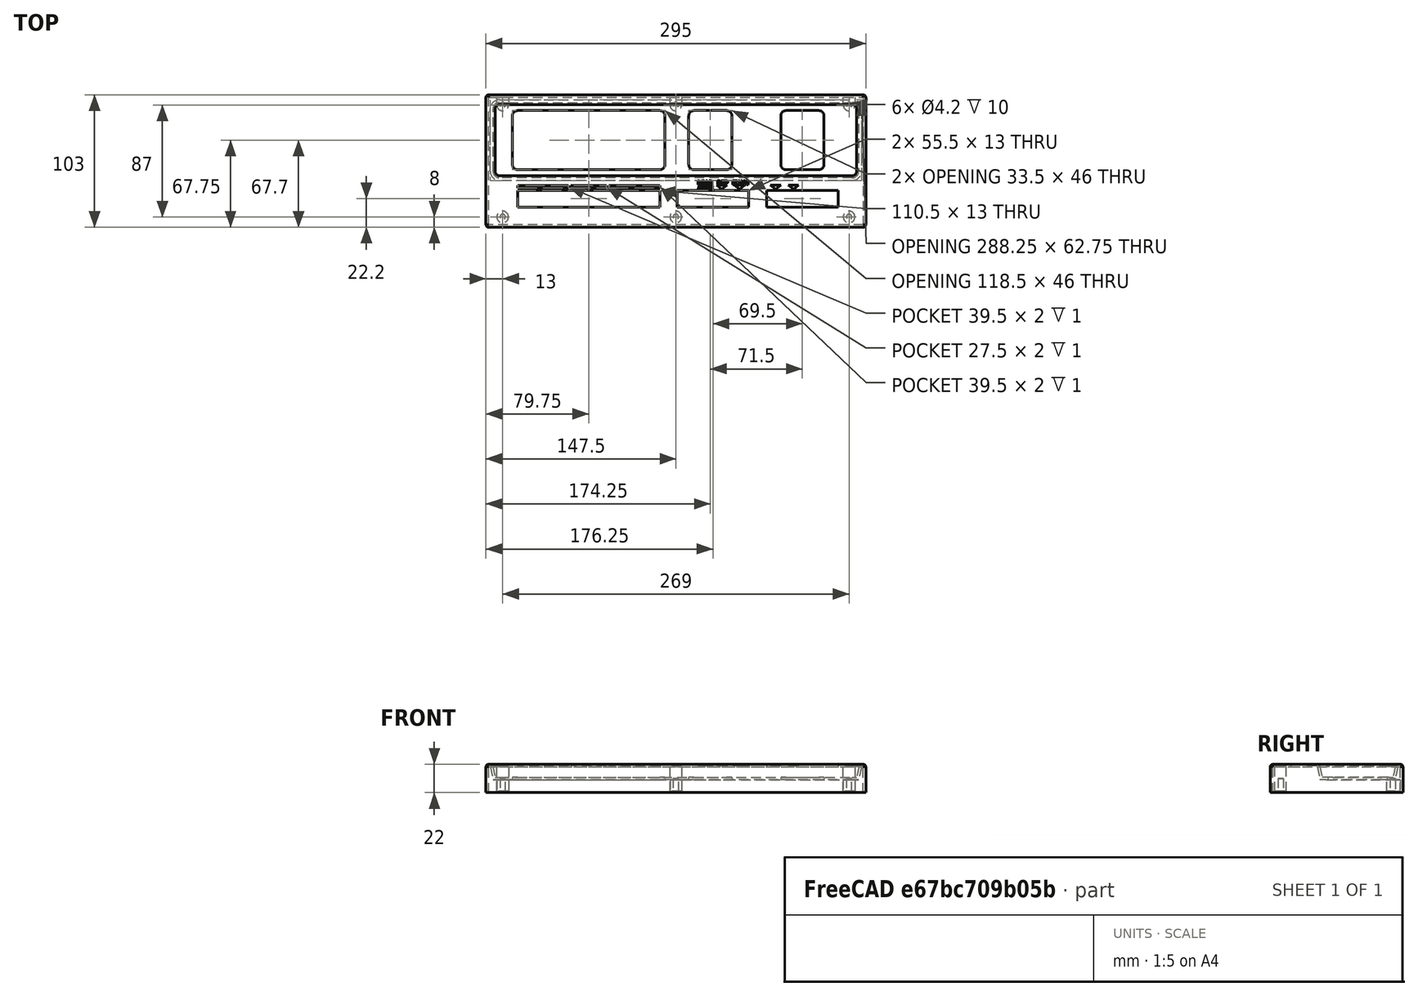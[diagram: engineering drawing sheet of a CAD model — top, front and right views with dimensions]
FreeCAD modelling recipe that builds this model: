
FCSTD DOCUMENT  (FreeCAD 0.21R33771 (Git))
Label: front panel
License: All rights reserved
LicenseURL: http://en.wikipedia.org/wiki/All_rights_reserved
objects: PartDesign::Pocket×8, Sketcher::SketchObject×7, PartDesign::LinearPattern×4, Part::Part2DObjectPython×4, PartDesign::Pad×3, TechDraw::DrawViewDimension×3, PartDesign::Draft×1, PartDesign::Thickness×1, PartDesign::MultiTransform×1, TechDraw::DrawSVGTemplate×1, PartDesign::Body×1, TechDraw::DrawProjGroupItem×1, TechDraw::DrawProjGroup×1, TechDraw::DrawPage×1
note: 48 computed .brp shape members not serialized (recipe doc carries the construction recipe); baked Part::Feature solids carry a one-line shape summary decoded from their .brp

FEATURE [Sketcher::SketchObject] Sketch
  FullyConstrained = true
  MapMode = 5
  Support = -> [XY_Plane]
  sketch-geometry (4):
    g0: LineSegment StartX=-145.5 StartY=49.5 StartZ=0 EndX=145.5 EndY=49.5 EndZ=0
    g1: LineSegment StartX=145.5 StartY=49.5 StartZ=0 EndX=145.5 EndY=-49.5 EndZ=0
    g2: LineSegment StartX=145.5 StartY=-49.5 StartZ=0 EndX=-145.5 EndY=-49.5 EndZ=0
    g3: LineSegment StartX=-145.5 StartY=-49.5 StartZ=0 EndX=-145.5 EndY=49.5 EndZ=0
  constraints (11):
    c: Coincident(g0,g1)
    c: Coincident(g1,g2)
    c: Coincident(g2,g3)
    c: Coincident(g3,g0)
    c: Horizontal(g0)
    c: Horizontal(g2)
    c: Vertical(g1)
    c: Vertical(g3)
    c: Symmetric(g1,g0,g-1)
    c: DistanceY(g3,g3) = 99
    c: DistanceX(g0,g0) = 291
FEATURE [PartDesign::Pad] Pad
  Direction = (0,0,1)
  Length = 20
  Length2 = 10
  Profile = -> Sketch
  ReferenceAxis = -> Sketch [N_Axis]
  Type = 0
FEATURE [Sketcher::SketchObject] Sketch001
  FullyConstrained = true
  MapMode = 5
  Placement = pos=(0,0,20) rot=(0,0,1;0rad)
  Support = -> [Pad]
  sketch-geometry (10):
    g0: ArcOfCircle CenterX=-137 CenterY=40.5 CenterZ=0 NormalX=0 NormalY=0 NormalZ=1 AngleXU=0 Radius=5 StartAngle=1.5708 EndAngle=3.14159
    g1: LineSegment StartX=-137 StartY=45.5 StartZ=0 EndX=137 EndY=45.5 EndZ=0
    g2: ArcOfCircle CenterX=137 CenterY=40.5 CenterZ=0 NormalX=0 NormalY=0 NormalZ=1 AngleXU=0 Radius=5 StartAngle=5e-16 EndAngle=1.5708
    g3: LineSegment StartX=142 StartY=40.5 StartZ=0 EndX=142 EndY=-8 EndZ=0
    g4: ArcOfCircle CenterX=137 CenterY=-8 CenterZ=0 NormalX=0 NormalY=0 NormalZ=1 AngleXU=0 Radius=5 StartAngle=4.71239 EndAngle=6.28319
    g5: LineSegment StartX=137 StartY=-13 StartZ=0 EndX=-137 EndY=-13 EndZ=0
    g6: ArcOfCircle CenterX=-137 CenterY=-8 CenterZ=0 NormalX=0 NormalY=0 NormalZ=1 AngleXU=0 Radius=5 StartAngle=3.14159 EndAngle=4.71239
    g7: LineSegment StartX=-142 StartY=-8 StartZ=0 EndX=-142 EndY=40.5 EndZ=0
    g8: GeomPoint X=-142 Y=45.5 Z=0
    g9: GeomPoint X=142 Y=-13 Z=0
  constraints (23):
    c: Tangent(g0,g1) = 1.5708
    c: Tangent(g1,g2) = 1.5708
    c: Tangent(g2,g3) = 1.5708
    c: Tangent(g3,g4) = 1.5708
    c: Tangent(g4,g5) = 1.5708
    c: Tangent(g5,g6) = 1.5708
    c: Tangent(g6,g7) = 1.5708
    c: Tangent(g7,g0) = 1.5708
    c: Horizontal(g1)
    c: Horizontal(g5)
    c: Vertical(g3)
    c: Vertical(g7)
    c: Equal(g2,g4)
    c: Equal(g4,g6)
    c: PointOnObject(g8,g1)
    c: PointOnObject(g8,g7)
    c: PointOnObject(g9,g3)
    c: PointOnObject(g9,g5)
    c: Diameter(g2) = 10
    c: DistanceX(g0,g2) = 284
    c: Symmetric(g0,g2,g-2)
    c: DistanceY(g-1,g0) = 45.5
    c: DistanceY(g5,g-1) = 13
FEATURE [PartDesign::Pocket] Pocket
  BaseFeature = -> Pad
  Direction = (0,0,-1)
  Length = 10
  Length2 = 5
  Profile = -> Sketch001
  ReferenceAxis = -> Sketch001 [N_Axis]
  Type = 0
FEATURE [PartDesign::Draft] Draft
  Angle = 12
  Base = -> Pocket [Face10]
  BaseFeature = -> Pocket
  NeutralPlane = -> Pocket [Face15]
  SupportTransform = false
FEATURE [PartDesign::Thickness] Thickness
  Base = -> Draft [Face4]
  BaseFeature = -> Draft
  Intersection = false
  Join = 0
  Mode = 0
  SupportTransform = false
  Value = 2
FEATURE [Sketcher::SketchObject] Sketch002
  FullyConstrained = true
  MapMode = 5
  Placement = pos=(0,0,22) rot=(0,0,1;0rad)
  Support = -> [Thickness]
  sketch-geometry (42):
    g0: LineSegment StartX=-123 StartY=-22.8 StartZ=0 EndX=-12.5 EndY=-22.8 EndZ=0
    g1: LineSegment StartX=-12.5 StartY=-22.8 StartZ=0 EndX=-12.5 EndY=-35.8 EndZ=0
    g2: LineSegment StartX=-12.5 StartY=-35.8 StartZ=0 EndX=-123 EndY=-35.8 EndZ=0
    g3: LineSegment StartX=-123 StartY=-35.8 StartZ=0 EndX=-123 EndY=-22.8 EndZ=0
    g4: LineSegment StartX=1 StartY=-22.8 StartZ=0 EndX=56.5 EndY=-22.8 EndZ=0
    g5: LineSegment StartX=56.5 StartY=-22.8 StartZ=0 EndX=56.5 EndY=-35.8 EndZ=0
    g6: LineSegment StartX=56.5 StartY=-35.8 StartZ=0 EndX=1 EndY=-35.8 EndZ=0
    g7: LineSegment StartX=1 StartY=-35.8 StartZ=0 EndX=1 EndY=-22.8 EndZ=0
    g8: LineSegment StartX=70.5 StartY=-22.8 StartZ=0 EndX=126 EndY=-22.8 EndZ=0
    g9: LineSegment StartX=126 StartY=-22.8 StartZ=0 EndX=126 EndY=-35.8 EndZ=0
    g10: LineSegment StartX=126 StartY=-35.8 StartZ=0 EndX=70.5 EndY=-35.8 EndZ=0
    g11: LineSegment StartX=70.5 StartY=-35.8 StartZ=0 EndX=70.5 EndY=-22.8 EndZ=0
    g12: ArcOfCircle CenterX=-123 CenterY=35.2 CenterZ=0 NormalX=0 NormalY=0 NormalZ=1 AngleXU=0 Radius=4 StartAngle=1.5708 EndAngle=3.14159
    g13: LineSegment StartX=-123 StartY=39.2 StartZ=0 EndX=-12.5 EndY=39.2 EndZ=0
    g14: ArcOfCircle CenterX=-12.5 CenterY=35.2 CenterZ=0 NormalX=0 NormalY=0 NormalZ=1 AngleXU=0 Radius=4 StartAngle=1e-15 EndAngle=1.5708
    g15: LineSegment StartX=-8.5 StartY=35.2 StartZ=0 EndX=-8.5 EndY=-2.8 EndZ=0
    g16: ArcOfCircle CenterX=-12.5 CenterY=-2.8 CenterZ=0 NormalX=0 NormalY=0 NormalZ=1 AngleXU=0 Radius=4 StartAngle=4.71239 EndAngle=6.28319
    g17: LineSegment StartX=-12.5 StartY=-6.8 StartZ=0 EndX=-123 EndY=-6.8 EndZ=0
    g18: ArcOfCircle CenterX=-123 CenterY=-2.8 CenterZ=0 NormalX=0 NormalY=0 NormalZ=1 AngleXU=0 Radius=4 StartAngle=3.14159 EndAngle=4.71239
    g19: LineSegment StartX=-127 StartY=-2.8 StartZ=0 EndX=-127 EndY=35.2 EndZ=0
    g20: GeomPoint X=-127 Y=39.2 Z=0
    g21: GeomPoint X=-8.5 Y=-6.8 Z=0
    g22: ArcOfCircle CenterX=14 CenterY=35.2 CenterZ=0 NormalX=0 NormalY=0 NormalZ=1 AngleXU=0 Radius=4 StartAngle=1.5708 EndAngle=3.14159
    g23: LineSegment StartX=14 StartY=39.2 StartZ=0 EndX=39.5 EndY=39.2 EndZ=0
    g24: ArcOfCircle CenterX=39.5 CenterY=35.2 CenterZ=0 NormalX=0 NormalY=0 NormalZ=1 AngleXU=0 Radius=4 StartAngle=1e-15 EndAngle=1.5708
    g25: LineSegment StartX=43.5 StartY=35.2 StartZ=0 EndX=43.5 EndY=-2.8 EndZ=0
    g26: ArcOfCircle CenterX=39.5 CenterY=-2.8 CenterZ=0 NormalX=0 NormalY=0 NormalZ=1 AngleXU=0 Radius=4 StartAngle=4.71239 EndAngle=6.28319
    g27: LineSegment StartX=39.5 StartY=-6.8 StartZ=0 EndX=14 EndY=-6.8 EndZ=0
    g28: ArcOfCircle CenterX=14 CenterY=-2.8 CenterZ=0 NormalX=0 NormalY=0 NormalZ=1 AngleXU=0 Radius=4 StartAngle=3.14159 EndAngle=4.71239
    g29: LineSegment StartX=10 StartY=-2.8 StartZ=0 EndX=10 EndY=35.2 EndZ=0
    g30: GeomPoint X=10 Y=39.2 Z=0
    g31: GeomPoint X=43.5 Y=-6.8 Z=0
    g32: ArcOfCircle CenterX=85.5 CenterY=35.2 CenterZ=0 NormalX=0 NormalY=0 NormalZ=1 AngleXU=0 Radius=4 StartAngle=1.5708 EndAngle=3.14159
    g33: LineSegment StartX=85.5 StartY=39.2 StartZ=0 EndX=111 EndY=39.2 EndZ=0
    g34: ArcOfCircle CenterX=111 CenterY=35.2 CenterZ=0 NormalX=0 NormalY=0 NormalZ=1 AngleXU=0 Radius=4 StartAngle=1e-15 EndAngle=1.5708
    g35: LineSegment StartX=115 StartY=35.2 StartZ=0 EndX=115 EndY=-2.8 EndZ=0
    g36: ArcOfCircle CenterX=111 CenterY=-2.8 CenterZ=0 NormalX=0 NormalY=0 NormalZ=1 AngleXU=0 Radius=4 StartAngle=4.71239 EndAngle=6.28319
    g37: LineSegment StartX=111 StartY=-6.8 StartZ=0 EndX=85.5 EndY=-6.8 EndZ=0
    g38: ArcOfCircle CenterX=85.5 CenterY=-2.8 CenterZ=0 NormalX=0 NormalY=0 NormalZ=1 AngleXU=0 Radius=4 StartAngle=3.14159 EndAngle=4.71239
    g39: LineSegment StartX=81.5 StartY=-2.8 StartZ=0 EndX=81.5 EndY=35.2 EndZ=0
    g40: GeomPoint X=81.5 Y=39.2 Z=0
    g41: GeomPoint X=115 Y=-6.8 Z=0
  constraints (108):
    c: Coincident(g0,g1)
    c: Coincident(g1,g2)
    c: Coincident(g2,g3)
    c: Coincident(g3,g0)
    c: Horizontal(g0)
    c: Horizontal(g2)
    c: Vertical(g1)
    c: Vertical(g3)
    c: Coincident(g4,g5)
    c: Coincident(g5,g6)
    c: Coincident(g6,g7)
    c: Coincident(g7,g4)
    c: Horizontal(g4)
    c: Horizontal(g6)
    c: Vertical(g5)
    c: Vertical(g7)
    c: Coincident(g8,g9)
    c: Coincident(g9,g10)
    c: Coincident(g10,g11)
    c: Coincident(g11,g8)
    c: Horizontal(g8)
    c: Horizontal(g10)
    c: Vertical(g9)
    c: Vertical(g11)
    c: Horizontal(g10,g5)
    c: Horizontal(g5,g1)
    c: Horizontal(g4,g0)
    c: Horizontal(g0,g8)
    c: DistanceY(g3,g3) = 13
    c: DistanceX(g2,g-1) = 123
    c: DistanceX(g0,g0) = 110.5
    c: DistanceY(g1,g-1) = 35.8
    c: DistanceX(g0,g4) = 13.5
    c: DistanceX(g4,g4) = 55.5
    c: DistanceX(g4,g8) = 14
    c: Equal(g8,g4)
    c: Tangent(g12,g13) = 1.5708
    c: Tangent(g13,g14) = 1.5708
    c: Tangent(g14,g15) = 1.5708
    c: Tangent(g15,g16) = 1.5708
    c: Tangent(g16,g17) = 1.5708
    c: Tangent(g17,g18) = 1.5708
    c: Tangent(g18,g19) = 1.5708
    c: Tangent(g19,g12) = 1.5708
    c: Horizontal(g13)
    c: Horizontal(g17)
    c: Vertical(g15)
    c: Vertical(g19)
    c: Equal(g12,g14)
    c: Equal(g14,g16)
    c: Equal(g16,g18)
    c: PointOnObject(g20,g13)
    c: PointOnObject(g20,g19)
    c: PointOnObject(g21,g15)
    c: PointOnObject(g21,g17)
    c: Radius(g12) = 4
    c: Vertical(g17,g0)
    c: Vertical(g16,g0)
    c: Tangent(g22,g23) = 1.5708
    c: Tangent(g23,g24) = 1.5708
    c: Tangent(g24,g25) = 1.5708
    c: Tangent(g25,g26) = 1.5708
    c: Tangent(g26,g27) = 1.5708
    c: Tangent(g27,g28) = 1.5708
    c: Tangent(g28,g29) = 1.5708
    c: Tangent(g29,g22) = 1.5708
    c: Horizontal(g23)
    c: Horizontal(g27)
    c: Vertical(g25)
    c: Vertical(g29)
    c: Equal(g22,g24)
    c: Equal(g24,g26)
    c: Equal(g26,g28)
    c: PointOnObject(g30,g23)
    c: PointOnObject(g30,g29)
    c: PointOnObject(g31,g25)
    c: PointOnObject(g31,g27)
    c: Equal(g26,g14)
    c: Horizontal(g22,g13)
    c: Horizontal(g27,g16)
    c: DistanceX(g26,g4) = 17
    c: DistanceX(g4,g27) = 13
    c: Tangent(g32,g33) = 1.5708
    c: Tangent(g33,g34) = 1.5708
    c: Tangent(g34,g35) = 1.5708
    c: Tangent(g35,g36) = 1.5708
    c: Tangent(g36,g37) = 1.5708
    c: Tangent(g37,g38) = 1.5708
    c: Tangent(g38,g39) = 1.5708
    c: Tangent(g39,g32) = 1.5708
    c: Horizontal(g33)
    c: Horizontal(g37)
    c: Vertical(g35)
    c: Vertical(g39)
    c: Equal(g32,g34)
    c: Equal(g34,g36)
    c: Equal(g36,g38)
    c: PointOnObject(g40,g33)
    c: PointOnObject(g40,g39)
    c: PointOnObject(g41,g35)
    c: PointOnObject(g41,g37)
    c: Horizontal(g23,g32)
    c: Equal(g32,g24)
    c: DistanceX(g36,g8) = 15
    c: Equal(g27,g37)
    c: DistanceY(g8,g35) = 20
    c: DistanceY(g8,g33) = 62
    c: Horizontal(g37,g16)
FEATURE [PartDesign::Pocket] Pocket001  label="Switch cut out"
  BaseFeature = -> Thickness
  Direction = (0,0,-1)
  Length = 5
  Length2 = 5
  Profile = -> Sketch002
  ReferenceAxis = -> Sketch002 [N_Axis]
  Type = 1
FEATURE [Sketcher::SketchObject] Sketch003
  FullyConstrained = true
  MapMode = 5
  Placement = pos=(0,0,20) rot=(1,0,0;3.14159rad)
  Support = -> [Pocket001]
  sketch-geometry (1):
    g0: Circle CenterX=-134.5 CenterY=43.5 CenterZ=0 NormalX=0 NormalY=0 NormalZ=1 AngleXU=0 Radius=4.5
  constraints (3):
    c: DistanceY(g-1,g0) = 43.5
    c: DistanceX(g0,g-1) = 134.5
    c: Diameter(g0) = 9
FEATURE [PartDesign::Pad] Pad001
  BaseFeature = -> Pocket001
  Direction = (0,0,-1)
  Length = 19
  Length2 = 10
  Profile = -> Sketch003
  ReferenceAxis = -> Sketch003 [N_Axis]
  Type = 0
FEATURE [PartDesign::LinearPattern] LinearPattern
  BaseFeature = -> Pad001
  Direction = -> Sketch003 [H_Axis]
  Length = 269
  Occurrences = 3
  Originals = -> [Pad001]
FEATURE [Sketcher::SketchObject] Sketch004
  ExternalGeometry = -> [LinearPattern]
  FullyConstrained = true
  MapMode = 5
  Placement = pos=(0,0,10) rot=(1,0,0;3.14159rad)
  Support = -> [LinearPattern]
  sketch-geometry (4):
    g0: ArcOfCircle CenterX=-134.5 CenterY=-43.5 CenterZ=0 NormalX=0 NormalY=0 NormalZ=1 AngleXU=0 Radius=4.5 StartAngle=-9e-16 EndAngle=3.14159
    g1: LineSegment StartX=-139 StartY=-43.5 StartZ=0 EndX=-139 EndY=-49.5 EndZ=0
    g2: LineSegment StartX=-139 StartY=-49.5 StartZ=0 EndX=-130 EndY=-49.5 EndZ=0
    g3: LineSegment StartX=-130 StartY=-49.5 StartZ=0 EndX=-130 EndY=-43.5 EndZ=0
  constraints (11):
    c: Tangent(g0,g1) = -1.5708
    c: Coincident(g1,g2)
    c: PointOnObject(g2,g-3)
    c: Horizontal(g2)
    c: Coincident(g2,g3)
    c: Vertical(g3)
    c: Vertical(g1)
    c: Diameter(g0) = 9
    c: DistanceX(g0,g-1) = 134.5
    c: DistanceY(g0,g-1) = 43.5
    c: Tangent(g3,g0) = -1.5708
FEATURE [PartDesign::Pad] Pad002
  BaseFeature = -> LinearPattern
  Direction = (0,0,-1)
  Length = 9
  Length2 = 10
  Profile = -> Sketch004
  ReferenceAxis = -> Sketch004 [N_Axis]
  Type = 0
FEATURE [PartDesign::LinearPattern] LinearPattern001
  BaseFeature = -> Pad002
  Direction = -> Sketch004 [H_Axis]
  Length = 269
  Occurrences = 3
  Originals = -> [Pad002]
FEATURE [Sketcher::SketchObject] Sketch005
  ExternalGeometry = -> [LinearPattern001]
  FullyConstrained = true
  MapMode = 5
  Placement = pos=(0,0,1) rot=(1,0,0;3.14159rad)
  Support = -> [LinearPattern001]
  sketch-geometry (1):
    g0: Circle CenterX=-134.5 CenterY=43.5 CenterZ=0 NormalX=0 NormalY=0 NormalZ=1 AngleXU=0 Radius=2.1
  constraints (2):
    c: Coincident(g0,g-3)
    c: Diameter(g0) = 4.2
FEATURE [PartDesign::Pocket] Pocket002
  BaseFeature = -> LinearPattern001
  Direction = (0,0,1)
  Length = 10
  Length2 = 5
  Profile = -> Sketch005
  ReferenceAxis = -> Sketch005 [N_Axis]
  Type = 0
FEATURE [PartDesign::LinearPattern] LinearPattern002
  Direction = -> Sketch005 [H_Axis]
  Length = 269
  Occurrences = 3
FEATURE [PartDesign::LinearPattern] LinearPattern003
  Direction = -> Sketch005 [V_Axis]
  Length = 87
  Occurrences = 2
  Reversed = true
FEATURE [PartDesign::MultiTransform] MultiTransform
  BaseFeature = -> Pocket002
  Originals = -> [Pocket002]
  Transformations = -> [LinearPattern002,LinearPattern003]
FEATURE [TechDraw::DrawSVGTemplate] Template
  EditableTexts = APPROVER_NAME=APPROVER NAME; AUTHOR_NAME=AUTHOR NAME; DATE=YYYY-MM-DD; DN=DN; DOCUMENT_TYPE=Mechanical assembly drawing; OWNER_NAME=OWNER NAME; PM=PM; PN=PN; REVISION=REV A; RIGHTS=(R) DO NOT DUPLICATE THIS DRAWING TO THIRD PARTIES WITHOUT OWNER'S PERMISSION!; SCALE=M x:x; SHEET=99 of 99; SIZE=A3; TITLELINE-1=FreeCAD; TOLERANCE=+/- ?
  Height = 297
  Orientation = 1
  Template = /Applications/FreeCAD.app/Contents/Resources/share/Mod/TechDraw/Templates/A3_Landscape_ISO7200_Pep.svg
  Width = 420
FEATURE [Sketcher::SketchObject] Sketch006
  ExternalGeometry = -> [MultiTransform]
  FullyConstrained = true
  MapMode = 5
  Placement = pos=(0,0,22) rot=(0,0,1;0rad)
  Support = -> [MultiTransform]
  sketch-geometry (28):
    g0: LineSegment StartX=-123 StartY=-19.098 StartZ=0 EndX=-83.5 EndY=-19.098 EndZ=0
    g1: LineSegment StartX=-83.5 StartY=-19.098 StartZ=0 EndX=-83.5 EndY=-21.098 EndZ=0
    g2: LineSegment StartX=-83.5 StartY=-21.098 StartZ=0 EndX=-123 EndY=-21.098 EndZ=0
    g3: LineSegment StartX=-123 StartY=-21.098 StartZ=0 EndX=-123 EndY=-19.098 EndZ=0
    g4: LineSegment StartX=-81.5 StartY=-19.098 StartZ=0 EndX=-54 EndY=-19.098 EndZ=0
    g5: LineSegment StartX=-54 StartY=-19.098 StartZ=0 EndX=-54 EndY=-21.098 EndZ=0
    g6: LineSegment StartX=-54 StartY=-21.098 StartZ=0 EndX=-81.5 EndY=-21.098 EndZ=0
    g7: LineSegment StartX=-81.5 StartY=-21.098 StartZ=0 EndX=-81.5 EndY=-19.098 EndZ=0
    g8: LineSegment StartX=-52 StartY=-19.098 StartZ=0 EndX=-12.5 EndY=-19.098 EndZ=0
    g9: LineSegment StartX=-12.5 StartY=-19.098 StartZ=0 EndX=-12.5 EndY=-21.098 EndZ=0
    g10: LineSegment StartX=-12.5 StartY=-21.098 StartZ=0 EndX=-52 EndY=-21.098 EndZ=0
    g11: LineSegment StartX=-52 StartY=-21.098 StartZ=0 EndX=-52 EndY=-19.098 EndZ=0
    g12: LineSegment StartX=53.5 StartY=-18.8 StartZ=0 EndX=45.5 EndY=-18.8 EndZ=0
    g13: LineSegment StartX=45.5 StartY=-18.8 StartZ=0 EndX=49.5 EndY=-21.8 EndZ=0
    g14: LineSegment StartX=49.5 StartY=-21.8 StartZ=0 EndX=53.5 EndY=-18.8 EndZ=0
    g15: Circle CenterX=49.5 CenterY=-17.6333 CenterZ=0 NormalX=0 NormalY=0 NormalZ=1 AngleXU=0 Radius=4.16667
    g16: LineSegment StartX=35.7 StartY=-21.8 StartZ=0 EndX=39.7 EndY=-18.8 EndZ=0
    g17: LineSegment StartX=39.7 StartY=-18.8 StartZ=0 EndX=31.7 EndY=-18.8 EndZ=0
    g18: LineSegment StartX=31.7 StartY=-18.8 StartZ=0 EndX=35.7 EndY=-21.8 EndZ=0
    g19: Circle CenterX=35.7 CenterY=-17.6333 CenterZ=0 NormalX=0 NormalY=0 NormalZ=1 AngleXU=0 Radius=4.16667
    g20: LineSegment StartX=77.5 StartY=-21.8 StartZ=0 EndX=81.5 EndY=-18.8 EndZ=0
    g21: LineSegment StartX=81.5 StartY=-18.8 StartZ=0 EndX=73.5 EndY=-18.8 EndZ=0
    g22: LineSegment StartX=73.5 StartY=-18.8 StartZ=0 EndX=77.5 EndY=-21.8 EndZ=0
    g23: Circle CenterX=77.5 CenterY=-17.6333 CenterZ=0 NormalX=0 NormalY=0 NormalZ=1 AngleXU=0 Radius=4.16667
    g24: LineSegment StartX=91.3 StartY=-21.8 StartZ=0 EndX=95.3 EndY=-18.8 EndZ=0
    g25: LineSegment StartX=95.3 StartY=-18.8 StartZ=0 EndX=87.3 EndY=-18.8 EndZ=0
    g26: LineSegment StartX=87.3 StartY=-18.8 StartZ=0 EndX=91.3 EndY=-21.8 EndZ=0
    g27: Circle CenterX=91.3 CenterY=-17.6333 CenterZ=0 NormalX=0 NormalY=0 NormalZ=1 AngleXU=0 Radius=4.16667
  constraints (84):
    c: Coincident(g0,g1)
    c: Coincident(g1,g2)
    c: Coincident(g2,g3)
    c: Coincident(g3,g0)
    c: Horizontal(g0)
    c: Horizontal(g2)
    c: Vertical(g1)
    c: Vertical(g3)
    c: Coincident(g4,g5)
    c: Coincident(g5,g6)
    c: Coincident(g6,g7)
    c: Coincident(g7,g4)
    c: Horizontal(g4)
    c: Horizontal(g6)
    c: Vertical(g5)
    c: Vertical(g7)
    c: Coincident(g8,g9)
    c: Coincident(g9,g10)
    c: Coincident(g10,g11)
    c: Coincident(g11,g8)
    c: Horizontal(g8)
    c: Horizontal(g10)
    c: Vertical(g9)
    c: Vertical(g11)
    c: DistanceY(g3,g3) = 2
    c: Vertical(g2,g-3)
    c: Equal(g8,g0)
    c: Horizontal(g6,g1)
    c: Horizontal(g1,g10)
    c: Horizontal(g8,g4)
    c: Horizontal(g4,g0)
    c: Vertical(g9,g-4)
    c: DistanceY(g-3,g2) = 1.702
    c: DistanceX(g0,g4) = 2
    c: DistanceX(g4,g8) = 2
    c: DistanceX(g8,g8) = 39.5
    c: Coincident(g12,g13)
    c: Coincident(g13,g14)
    c: Coincident(g14,g12)
    c: PointOnObject(g12,g15)
    c: PointOnObject(g13,g15)
    c: PointOnObject(g14,g15)
    c: Coincident(g16,g17)
    c: Coincident(g17,g18)
    c: Coincident(g18,g16)
    c: Equal(g16,g18)
    c: PointOnObject(g16,g19)
    c: PointOnObject(g17,g19)
    c: PointOnObject(g18,g19)
    c: Horizontal(g17)
    c: Horizontal(g12)
    c: Equal(g16,g13)
    c: DistanceX(g19,g15) = 13.8
    c: Equal(g17,g12)
    c: Horizontal(g16,g12)
    c: Equal(g14,g13)
    c: DistanceX(g17,g17) = 8
    c: DistanceY(g16,g16) = 3
    c: DistanceX(g13,g-5) = 7
    c: DistanceY(g-5,g13) = 1
    c: Coincident(g20,g21)
    c: Coincident(g21,g22)
    c: Coincident(g22,g20)
    c: Equal(g20,g22)
    c: PointOnObject(g20,g23)
    c: PointOnObject(g21,g23)
    c: PointOnObject(g22,g23)
    c: Coincident(g24,g25)
    c: Coincident(g25,g26)
    c: Coincident(g26,g24)
    c: Equal(g24,g26)
    c: PointOnObject(g24,g27)
    c: PointOnObject(g25,g27)
    c: PointOnObject(g26,g27)
    c: Horizontal(g25,g20)
    c: Horizontal(g25)
    c: Horizontal(g21)
    c: DistanceX(g23,g27) = 13.8
    c: Equal(g21,g25)
    c: Equal(g25,g12)
    c: DistanceY(g20,g20) = 3
    c: Horizontal(g24,g20)
    c: Horizontal(g12,g21)
    c: DistanceX(g-6,g20) = 7
FEATURE [PartDesign::Pocket] Pocket003  label="Down arrows"
  BaseFeature = -> MultiTransform
  Direction = (0,0,-1)
  Length = 1
  Length2 = 5
  Profile = -> Sketch006
  ReferenceAxis = -> Sketch006 [N_Axis]
  Type = 0
FEATURE [Part::Part2DObjectPython] ShapeString  label="DEP"  # Draft 2D object (typed FeaturePython)
  FontFile = <userpath>/Downloads/roboto/Roboto-Black.ttf
  MakeFace = true
  Placement = pos=(32,-18.5,22) rot=(0,0,1;0rad)
  Size = 4
  String = DEP
  Tracking = 0
FEATURE [Part::Part2DObjectPython] ShapeString001  label="LOAD"  # Draft 2D object (typed FeaturePython)
  FontFile = <userpath>/Downloads/roboto/Roboto-Black.ttf
  MakeFace = true
  Placement = pos=(17,-18.5,22) rot=(0,0,1;0rad)
  Size = 4
  String = LOAD
  Tracking = 0
FEATURE [Part::Part2DObjectPython] ShapeString002  label="ADDR"  # Draft 2D object (typed FeaturePython)
  FontFile = <userpath>/Downloads/roboto/Roboto-Black.ttf
  MakeFace = true
  Placement = pos=(17,-22.25,22) rot=(0.987988,-0.125405,-0.090301;0rad)
  Size = 4
  String = ADDR
  Tracking = 0
FEATURE [PartDesign::Pocket] Pocket004  label="DEP Pocket"
  BaseFeature = -> Pocket003
  Direction = (0,0,-1)
  Length = 1
  Length2 = 5
  Profile = -> ShapeString
  ReferenceAxis = -> ShapeString [N_Axis]
  Type = 0
FEATURE [PartDesign::Pocket] Pocket005  label="Load Pocket"
  BaseFeature = -> Pocket004
  Direction = (0,0,-1)
  Length = 1
  Length2 = 5
  Profile = -> ShapeString001
  ReferenceAxis = -> ShapeString001 [N_Axis]
  Type = 0
FEATURE [PartDesign::Pocket] Pocket006  label="ADDR Pocket"
  BaseFeature = -> Pocket005
  Direction = (0,0,-1)
  Length = 1
  Length2 = 5
  Profile = -> ShapeString002
  ReferenceAxis = -> ShapeString002 [N_Axis]
  Type = 0
FEATURE [Part::Part2DObjectPython] ShapeString003  label="EXAM"  # Draft 2D object (typed FeaturePython)
  FontFile = <userpath>/Downloads/roboto/Roboto-Black.ttf
  MakeFace = true
  Placement = pos=(44,-18.5,22) rot=(0,0,1;0rad)
  Size = 4
  String = EXAM
  Tracking = 0
FEATURE [PartDesign::Pocket] Pocket007
  BaseFeature = -> Pocket006
  Direction = (0,0,-1)
  Length = 1
  Length2 = 5
  Profile = -> ShapeString003
  ReferenceAxis = -> ShapeString003 [N_Axis]
  Type = 0
FEATURE [PartDesign::Body] Body
  Group = -> [Sketch,Pad,Sketch001,Pocket,Draft,Thickness,Sketch002,Pocket001,Sketch003,Pad001,LinearPattern,Sketch004,Pad002,LinearPattern001,Sketch005,Pocket002,MultiTransform,LinearPattern002,LinearPattern003,Sketch006,Pocket003,ShapeString,ShapeString001,ShapeString002,Pocket004,Pocket005,Pocket006,ShapeString003,Pocket007]
  Origin = -> Origin
  Tip = -> Pocket007
FEATURE [TechDraw::DrawProjGroupItem] ProjItem  label="Front"
  CoarseView = false
  Direction = (0,0,1)
  Focus = 100
  HardHidden = false
  IsoCount = 0
  IsoHidden = false
  IsoVisible = false
  LockPosition = true
  Perspective = false
  Rotation = 0
  RotationVector = (1,0,0)
  ScaleType = 2
  ScrubCount = 0
  SeamHidden = false
  SeamVisible = true
  SmoothHidden = false
  SmoothVisible = true
  Source = -> [Body]
  Type = 0
  X = 0
  XDirection = (1,0,0)
  Y = 0
FEATURE [TechDraw::DrawProjGroup] ProjGroup
  Anchor = -> ProjItem
  AutoDistribute = true
  LockPosition = false
  ProjectionType = 0
  Rotation = 0
  ScaleType = 0
  Source = -> [Body]
  Views = -> [ProjItem]
  X = 210
  Y = 148.5
  spacingX = 15
  spacingY = 15
FEATURE [TechDraw::DrawViewDimension] Dimension001
  AngleOverride = false
  Arbitrary = false
  ArbitraryTolerances = false
  EqualTolerance = true
  ExtensionAngle = 0
  FormatSpec = %.3f
  FormatSpecOverTolerance = %+.3f
  FormatSpecUnderTolerance = %+.3f
  Inverted = false
  LineAngle = 0
  LockPosition = false
  MeasureType = 1
  OverTolerance = 0
  References2D = -> [ProjItem]
  Rotation = 0
  ScaleType = 0
  TheoreticalExact = false
  Type = 2
  UnderTolerance = 0
  X = 168.608
  Y = 20.4136
FEATURE [TechDraw::DrawViewDimension] Dimension002
  AngleOverride = false
  Arbitrary = false
  ArbitraryTolerances = false
  EqualTolerance = true
  ExtensionAngle = 0
  FormatSpec = R%.3f
  FormatSpecOverTolerance = %+.3f
  FormatSpecUnderTolerance = %+.3f
  Inverted = false
  LineAngle = 0
  LockPosition = false
  MeasureType = 1
  OverTolerance = 0
  References2D = -> [ProjItem]
  Rotation = 0
  ScaleType = 0
  TheoreticalExact = false
  Type = 4
  UnderTolerance = 0
  X = -162.459
  Y = 43.8237
FEATURE [TechDraw::DrawViewDimension] Dimension
  AngleOverride = false
  Arbitrary = false
  ArbitraryTolerances = false
  EqualTolerance = true
  ExtensionAngle = 0
  FormatSpec = %.3f
  FormatSpecOverTolerance = %+.3f
  FormatSpecUnderTolerance = %+.3f
  Inverted = false
  LineAngle = 0
  LockPosition = false
  MeasureType = 1
  OverTolerance = 0
  References2D = -> [ProjItem]
  Rotation = 0
  ScaleType = 0
  TheoreticalExact = false
  Type = 1
  UnderTolerance = 0
  X = -6.9642
  Y = 88.1732
FEATURE [TechDraw::DrawPage] Page
  KeepUpdated = true
  NextBalloonIndex = 1
  ProjectionType = 0
  Template = -> Template
  Views = -> [ProjGroup,Dimension001,Dimension002,Dimension]
